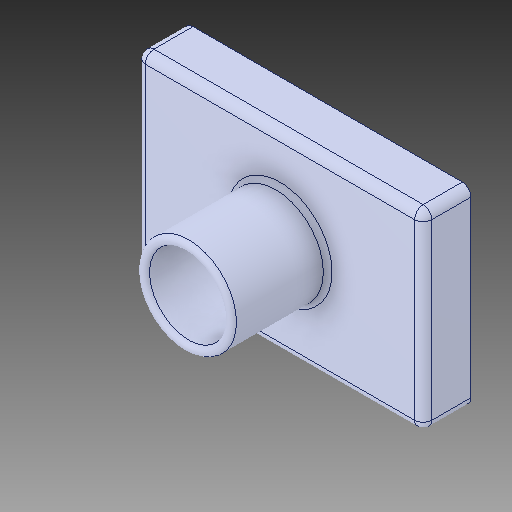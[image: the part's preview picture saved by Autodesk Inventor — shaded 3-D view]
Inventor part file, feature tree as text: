
AUTODESK INVENTOR PART (.ipt)
format: ipt  version: 2018 (Build 220112000, 112)  size: 161,792 bytes
history: native  units: in
note: dims shown in document units (in); Inventor stores cm internally (conversion verified against a paired STEP export)
features: fillet x1
ambient origin geometry x8: Origin, YZ Plane, XZ Plane, XY Plane, X Axis, Y Axis, Z Axis, Center Point
bodies: Solid1 (feature_tree)
feature tree (1):
  fillet  "Fillet10"  [1 undecoded]
note: 1 required parameter value undecoded (feature->parameter linkage not recoverable at this tier; creation-order binding heuristic only, values carry confidence <= 0.55)
